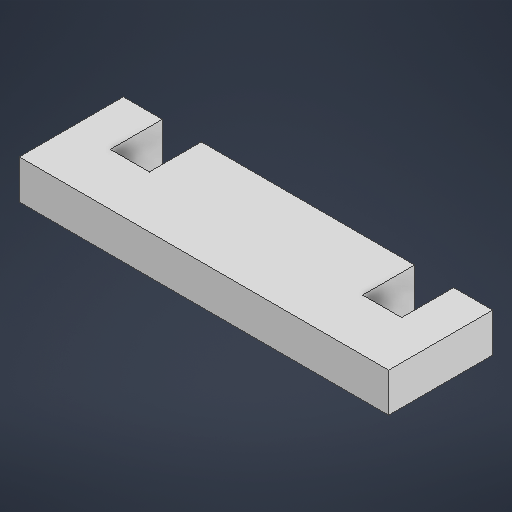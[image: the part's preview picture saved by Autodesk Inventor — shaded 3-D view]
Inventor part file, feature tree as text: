
AUTODESK INVENTOR PART (.ipt)
format: ipt  version: 2025.3 (Build 293356030, 356C)  size: 180,224 bytes
history: native  units: mm
features: other x1, extrude x1, sketch x1
ambient origin geometry x8: Origin, YZ Plane, XZ Plane, XY Plane, X Axis, Y Axis, Z Axis, Center Point
bodies: Body1 (feature_tree)
feature tree (3):
  other  "實體1"
  extrude  "擠出1"  Depth=4.0mm
  sketch  "草圖1"
